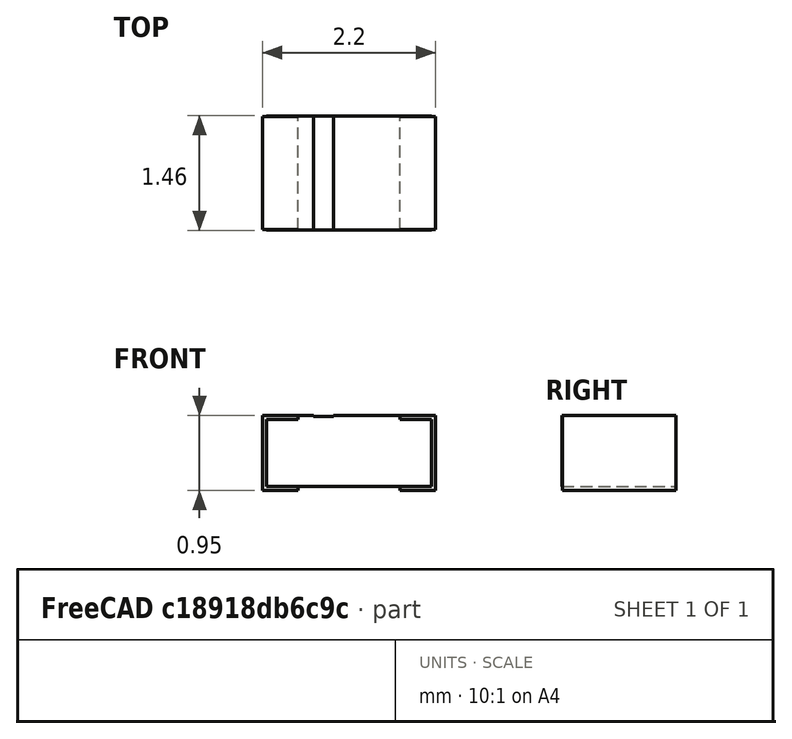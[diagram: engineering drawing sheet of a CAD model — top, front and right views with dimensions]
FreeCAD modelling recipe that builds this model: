
FCSTD DOCUMENT
Label: DIO_CHIP_2012X085
Comment: Taiwan Semiconductor TS4148RY
objects: Part::Box×5, Part::Cut×1, Part::MultiFuse×1
note: 7 computed .brp shape members not serialized (recipe doc carries the construction recipe); baked Part::Feature solids carry a one-line shape summary decoded from their .brp

FEATURE [Part::Box] chip
  Height = 0.85
  Length = 2.1
  Placement = pos=(-1.05,-0.725,0.05) rot=(0,0,1;0rad)
  Width = 1.45
FEATURE [Part::Box] plating_left
  Height = 0.95
  Length = 0.45
  Placement = pos=(-1.1,-0.72,0) rot=(0,0,1;0rad)
  Width = 1.44
FEATURE [Part::Box] plating_right
  Height = 0.95
  Length = 0.45
  Placement = pos=(0.65,-0.72,0) rot=(0,0,1;0rad)
  Width = 1.44
FEATURE [Part::Box] marking
  Height = 0.05
  Length = 1.3
  Placement = pos=(-0.65,-0.725,0.9) rot=(0,0,1;0rad)
  Width = 1.45
FEATURE [Part::Box] Box
  Height = 3
  Length = 0.25
  Placement = pos=(-0.45,-2,0.94) rot=(0,0,1;0rad)
  Width = 3
FEATURE [Part::Cut] Cut
  Base = -> marking
  Tool = -> Box
FEATURE [Part::MultiFuse] Fusion  label="DIO_CHIP"
  Shapes = -> [chip,plating_left,plating_right,Cut]
